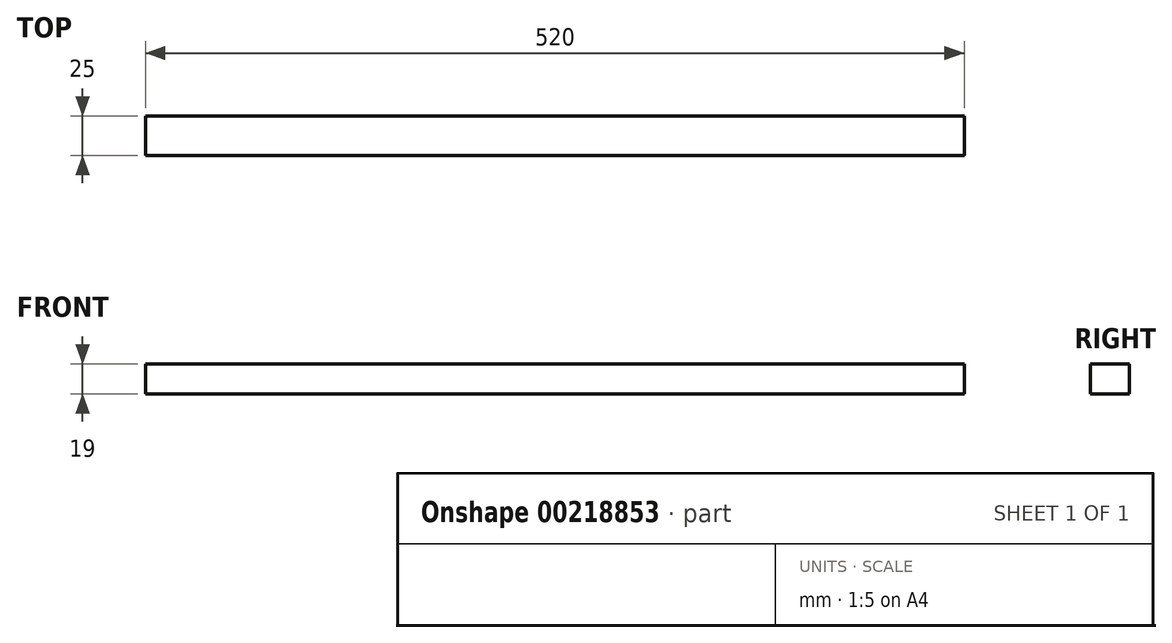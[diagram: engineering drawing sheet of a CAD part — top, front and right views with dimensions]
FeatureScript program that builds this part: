
annotation { "Feature Type Name" : "Feature", "Feature Type Description" : "" }
export const myFeature = defineFeature(function(context is Context, id is Id, definition is map)
    precondition{}
    {
        {
            var Q0;
            Q0=qCreatedBy(makeId("Front.planeOp"),FACE);
            var sketch = newSketch(context, id + "F0", { "sketchPlane" : qUnion([Q0])});
            skLineSegment(sketch, "E0.bottom", {"start": v(-274.43, -33.52) * mm, "end": v(245.57, -33.52) * mm});
            skLineSegment(sketch, "E0.top", {"start": v(-274.43, -52.52) * mm, "end": v(245.57, -52.52) * mm});
            skLineSegment(sketch, "E0.left", {"start": v(-274.43, -33.52) * mm, "end": v(-274.43, -52.52) * mm});
            skLineSegment(sketch, "E0.right", {"start": v(245.57, -33.52) * mm, "end": v(245.57, -52.52) * mm});
            skSolve(sketch);
        }
        {
            var Q0;
            Q0 = qSketchRegion(id + "F0", true);
            extrude(context, id + "F1", {"entities" : qUnion([Q0]), "depth" : 25 * mm});
        }
    });
